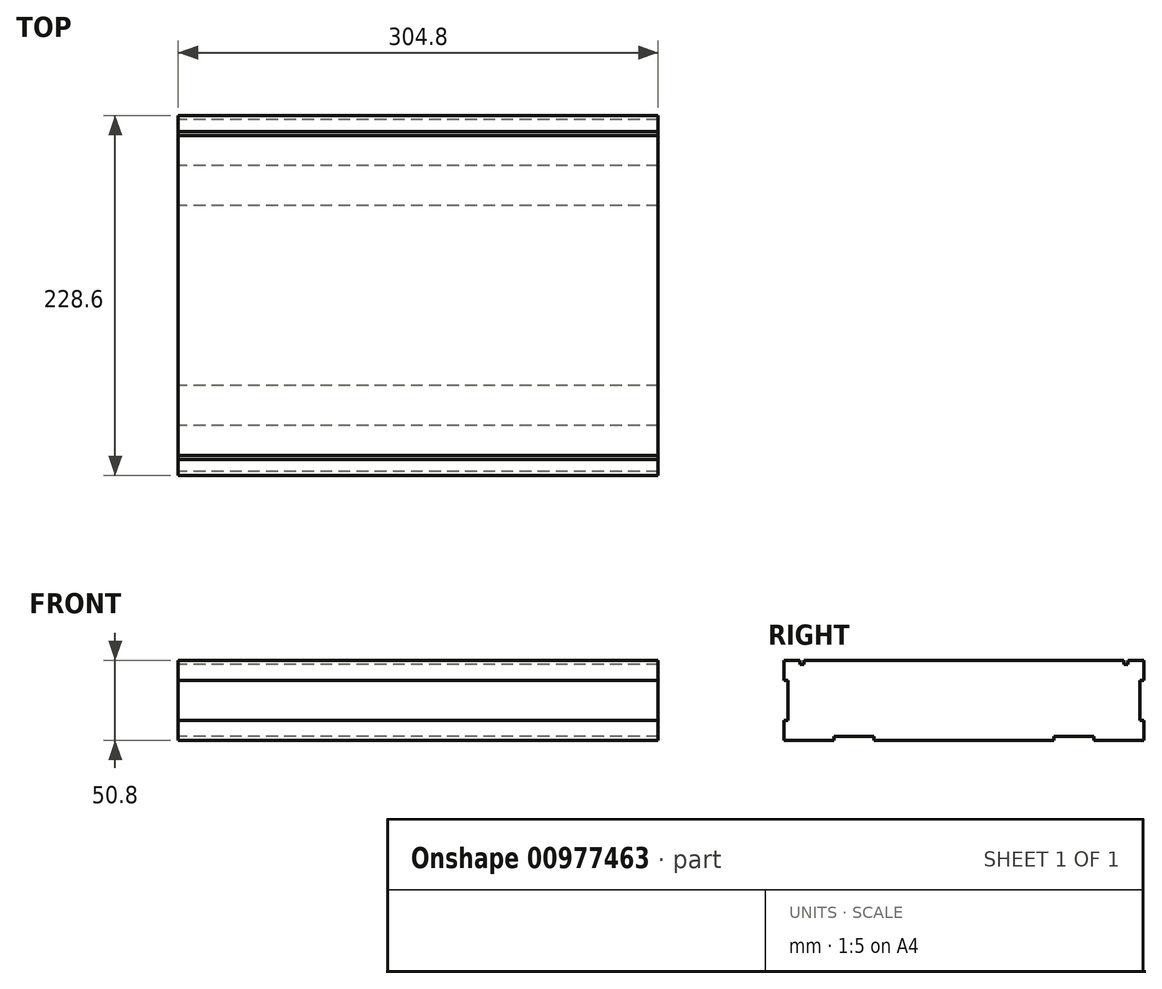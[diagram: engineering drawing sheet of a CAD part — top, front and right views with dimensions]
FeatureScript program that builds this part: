
annotation { "Feature Type Name" : "Feature", "Feature Type Description" : "" }
export const myFeature = defineFeature(function(context is Context, id is Id, definition is map)
    precondition{}
    {
        {
            var Q0;
            Q0=qCreatedBy(makeId("Right.planeOp"),FACE);
            var sketch = newSketch(context, id + "F0", { "sketchPlane" : qUnion([Q0])});
            skLineSegment(sketch, "E0", {"start": v(0, 0) * mm, "end": v(57.15, 0) * mm});
            skLineSegment(sketch, "E1", {"start": v(57.15, 0) * mm, "end": v(57.15, 2.54) * mm});
            skLineSegment(sketch, "E2", {"start": v(57.15, 2.54) * mm, "end": v(82.55, 2.54) * mm});
            skLineSegment(sketch, "E3", {"start": v(82.55, 2.54) * mm, "end": v(82.55, 0) * mm});
            skLineSegment(sketch, "E4", {"start": v(82.55, 0) * mm, "end": v(114.3, 0) * mm});
            skLineSegment(sketch, "E5", {"start": v(114.3, 0) * mm, "end": v(114.3, 12.7) * mm});
            skLineSegment(sketch, "E6", {"start": v(114.3, 12.7) * mm, "end": v(111.76, 12.7) * mm});
            skLineSegment(sketch, "E7", {"start": v(111.76, 12.7) * mm, "end": v(111.76, 38.1) * mm});
            skLineSegment(sketch, "E8", {"start": v(111.76, 38.1) * mm, "end": v(114.3, 38.1) * mm});
            skLineSegment(sketch, "E9", {"start": v(114.3, 38.1) * mm, "end": v(114.3, 50.8) * mm});
            skLineSegment(sketch, "E10", {"start": v(101.6, 48.26) * mm, "end": v(101.6, 50.8) * mm});
            skLineSegment(sketch, "E11", {"start": v(101.6, 50.8) * mm, "end": v(0, 50.8) * mm});
            skLineSegment(sketch, "E12.MirrorCS", {"start": v(0, 0) * mm, "end": v(-57.15, 0) * mm});
            skLineSegment(sketch, "E13.MirrorCS", {"start": v(-57.15, 0) * mm, "end": v(-57.15, 2.54) * mm});
            skLineSegment(sketch, "E14.MirrorCS", {"start": v(-82.55, 2.54) * mm, "end": v(-82.55, 0) * mm});
            skLineSegment(sketch, "E15.MirrorCS", {"start": v(-57.15, 2.54) * mm, "end": v(-82.55, 2.54) * mm});
            skLineSegment(sketch, "E16.MirrorCS", {"start": v(-82.55, 0) * mm, "end": v(-114.3, 0) * mm});
            skLineSegment(sketch, "E17.MirrorCS", {"start": v(-114.3, 0) * mm, "end": v(-114.3, 12.7) * mm});
            skLineSegment(sketch, "E18.MirrorCS", {"start": v(-111.76, 12.7) * mm, "end": v(-111.76, 38.1) * mm});
            skLineSegment(sketch, "E19.MirrorCS", {"start": v(-114.3, 38.1) * mm, "end": v(-114.3, 50.8) * mm});
            skLineSegment(sketch, "E20.MirrorCS", {"start": v(-101.6, 50.8) * mm, "end": v(0, 50.8) * mm});
            skLineSegment(sketch, "E21.MirrorCS", {"start": v(-101.6, 48.26) * mm, "end": v(-101.6, 50.8) * mm});
            skLineSegment(sketch, "E22.MirrorCS", {"start": v(-111.76, 38.1) * mm, "end": v(-114.3, 38.1) * mm});
            skLineSegment(sketch, "E23.MirrorCS", {"start": v(-114.3, 12.7) * mm, "end": v(-111.76, 12.7) * mm});
            skLineSegment(sketch, "E24", {"start": v(114.3, 50.8) * mm, "end": v(104.14, 50.8) * mm});
            skLineSegment(sketch, "E25", {"start": v(104.14, 50.8) * mm, "end": v(104.14, 48.26) * mm});
            skLineSegment(sketch, "E26", {"start": v(104.14, 48.26) * mm, "end": v(101.6, 48.26) * mm});
            skLineSegment(sketch, "E27.MirrorCS", {"start": v(-114.3, 50.8) * mm, "end": v(-104.14, 50.8) * mm});
            skLineSegment(sketch, "E28.MirrorCS", {"start": v(-104.14, 50.8) * mm, "end": v(-104.14, 48.26) * mm});
            skLineSegment(sketch, "E29.MirrorCS", {"start": v(-104.14, 48.26) * mm, "end": v(-101.6, 48.26) * mm});
            skSolve(sketch);
        }
        {
            var Q0;
            Q0 = qSketchRegion(id + "F0", true);
            extrude(context, id + "F1", {"entities" : qUnion([Q0]), "endBound" : BoundingType.SYMMETRIC, "depth" : 304.8 * mm, "offsetDistance" : 25.4 * mm});
        }
    });
